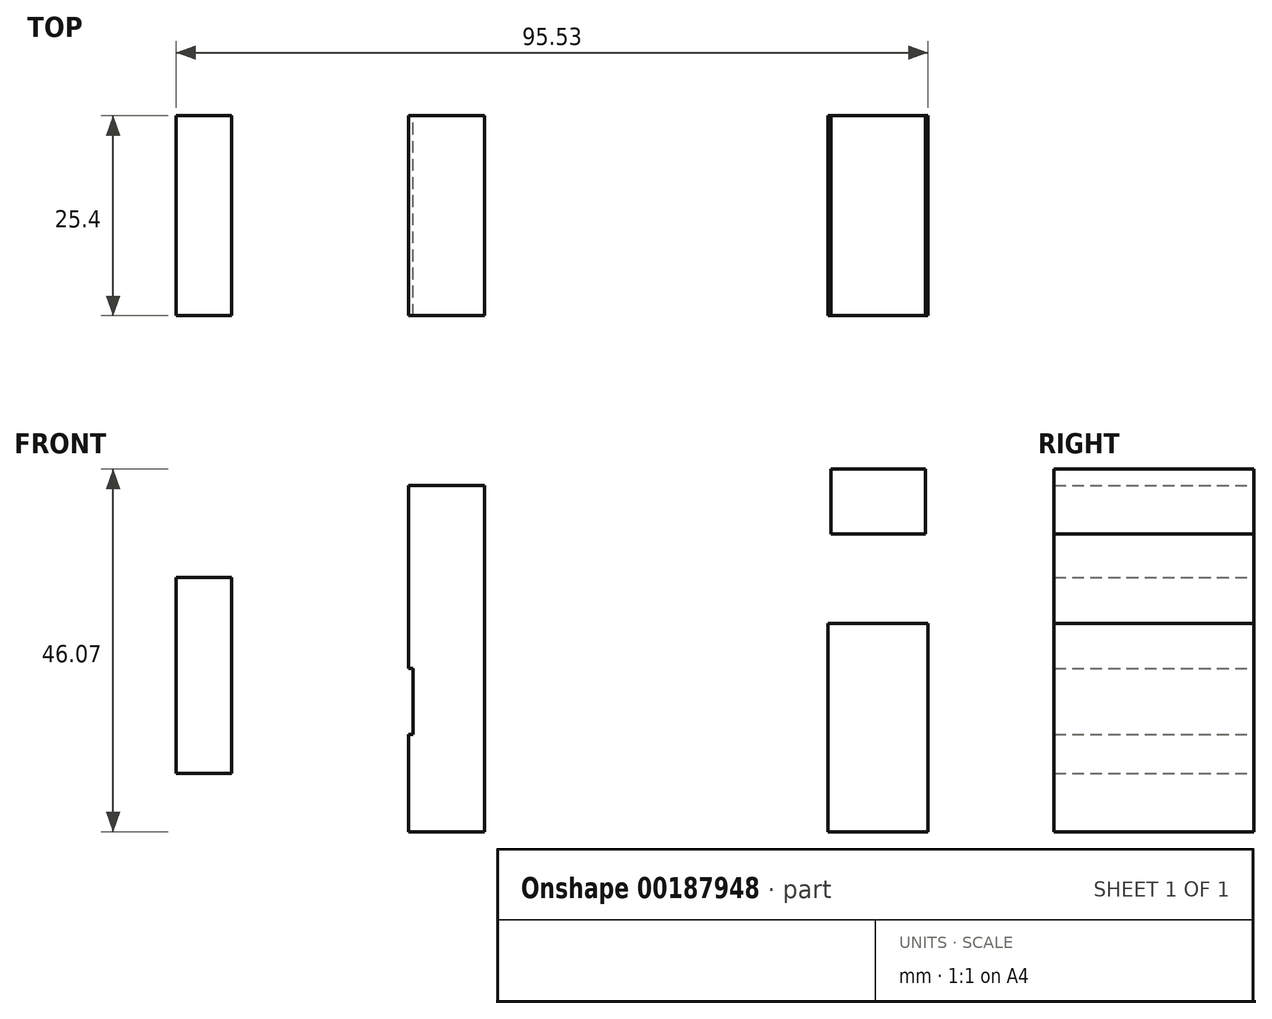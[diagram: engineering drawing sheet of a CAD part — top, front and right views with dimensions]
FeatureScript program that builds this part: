
annotation { "Feature Type Name" : "Feature", "Feature Type Description" : "" }
export const myFeature = defineFeature(function(context is Context, id is Id, definition is map)
    precondition{}
    {
        {
            var Q0;
            Q0=qCreatedBy(makeId("Front.planeOp"),FACE);
            var sketch = newSketch(context, id + "F0", { "sketchPlane" : qUnion([Q0])});
            skLineSegment(sketch, "E0.bottom", {"start": v(3.57, 3.45) * mm, "end": v(48.07, 3.45) * mm});
            skLineSegment(sketch, "E0.top", {"start": v(3.57, 146.1) * mm, "end": v(48.07, 146.1) * mm});
            skLineSegment(sketch, "E0.left", {"start": v(3.57, 3.45) * mm, "end": v(3.57, 146.1) * mm});
            skLineSegment(sketch, "E0.right", {"start": v(48.07, 3.45) * mm, "end": v(48.07, 146.1) * mm});
            skSolve(sketch);
        }
        {
            var Q0;
            Q0 = qSketchRegion(id + "F0", true);
            extrude(context, id + "F3", {"entities" : qUnion([Q0]), "depth" : 99.94 * mm});
        }
        {
            var Q0;
            Q0=makeQuery(id+"F3.opExtrude","SWEPT_BODY",BODY,{"disambiguationData":[OSD([sQuery(id+"F0.wireOp",EDGE,"E0.bottom"),sQuery(id+"F0.wireOp",EDGE,"E0.top"),sQuery(id+"F0.wireOp",EDGE,"E0.left"),sQuery(id+"F0.wireOp",EDGE,"E0.right")])]});
            deleteBodies(context, id + "F1", {"entities" : qUnion([Q0])});
        }
        {
            var Q0;
            Q0=qCreatedBy(makeId("Front.planeOp"),FACE);
            var sketch = newSketch(context, id + "F2", { "sketchPlane" : qUnion([Q0])});
            skLineSegment(sketch, "E1.bottom", {"start": v(-56.02, 40.73) * mm, "end": v(-48.98, 40.73) * mm});
            skLineSegment(sketch, "E1.top", {"start": v(-56.02, 15.81) * mm, "end": v(-48.98, 15.81) * mm});
            skLineSegment(sketch, "E1.left", {"start": v(-56.02, 40.73) * mm, "end": v(-56.02, 15.81) * mm});
            skLineSegment(sketch, "E1.right", {"start": v(-48.98, 40.73) * mm, "end": v(-48.98, 15.81) * mm});
            skLineSegment(sketch, "E2.bottom", {"start": v(-48.98, 20.8) * mm, "end": v(-25.95, 20.8) * mm});
            skLineSegment(sketch, "E2.top", {"start": v(-48.98, 29.15) * mm, "end": v(-25.95, 29.15) * mm});
            skLineSegment(sketch, "E2.left", {"start": v(-48.98, 20.8) * mm, "end": v(-48.98, 29.15) * mm});
            skLineSegment(sketch, "E2.right", {"start": v(-25.95, 20.8) * mm, "end": v(-25.95, 29.15) * mm});
            skLineSegment(sketch, "E3.bottom", {"start": v(-16.86, 52.43) * mm, "end": v(-26.47, 52.43) * mm});
            skLineSegment(sketch, "E3.top", {"start": v(-16.86, 8.42) * mm, "end": v(-26.47, 8.42) * mm});
            skLineSegment(sketch, "E3.left", {"start": v(-16.86, 52.43) * mm, "end": v(-16.86, 8.42) * mm});
            skLineSegment(sketch, "E3.right", {"start": v(-26.47, 52.43) * mm, "end": v(-26.47, 8.42) * mm});
            skLineSegment(sketch, "E4.bottom", {"start": v(27.14, 54.49) * mm, "end": v(39.18, 54.49) * mm});
            skLineSegment(sketch, "E4.top", {"start": v(27.14, 46.23) * mm, "end": v(39.18, 46.23) * mm});
            skLineSegment(sketch, "E4.left", {"start": v(27.14, 54.49) * mm, "end": v(27.14, 46.23) * mm});
            skLineSegment(sketch, "E4.right", {"start": v(39.18, 54.49) * mm, "end": v(39.18, 46.23) * mm});
            skLineSegment(sketch, "E5.bottom", {"start": v(26.8, 34.89) * mm, "end": v(39.5, 34.89) * mm});
            skLineSegment(sketch, "E5.top", {"start": v(26.8, 8.42) * mm, "end": v(39.5, 8.42) * mm});
            skLineSegment(sketch, "E5.left", {"start": v(26.8, 34.89) * mm, "end": v(26.8, 8.42) * mm});
            skLineSegment(sketch, "E5.right", {"start": v(39.5, 34.89) * mm, "end": v(39.5, 8.42) * mm});
            skSolve(sketch);
        }
        {
            var Q0;
            Q0=makeQuery(id+"F2.imprint","IMPRINT",FACE,{"disambiguationData":[TD([[makeQuery(id+"F2.imprint","IMPRINT",EDGE,{"derivedFrom":sQuery(id+"F2.wireOp",EDGE,"E5.bottom")}),-1.0]])]});
            var Q1;
            Q1=makeQuery(id+"F2.imprint","IMPRINT",FACE,{"disambiguationData":[TD([[makeQuery(id+"F2.imprint","IMPRINT",EDGE,{"derivedFrom":sQuery(id+"F2.wireOp",EDGE,"E4.bottom")}),-1.0]])]});
            var Q2;
            {var subQ0=sQuery(id+"F2.wireOp",EDGE,"E2.right");Q2=makeQuery(id+"F2.imprint","IMPRINT",FACE,{"disambiguationData":[TD([[makeQuery(id+"F2.imprint","IMPRINT",EDGE,{"derivedFrom":subQ0}),-1.0]])]});}
            var Q3;
            {var subQ1=sQuery(id+"F2.wireOp",EDGE,"E1.bottom");Q3=makeQuery(id+"F2.imprint","IMPRINT",FACE,{"disambiguationData":[TD([[makeQuery(id+"F2.imprint","IMPRINT",EDGE,{"derivedFrom":subQ1}),-1.0]])]});}
            var Q4;
            {var subQ0=sQuery(id+"F2.wireOp",EDGE,"E2.left");Q4=makeQuery(id+"F2.imprint","IMPRINT",FACE,{"disambiguationData":[TD([[makeQuery(id+"F2.imprint","IMPRINT",EDGE,{"derivedFrom":subQ0}),-1.0]])]});}
            extrude(context, id + "F4", {"entities" : qUnion([Q0, Q1, Q2, Q3, Q4]), "depth" : 25.4 * mm});
        }
    });
